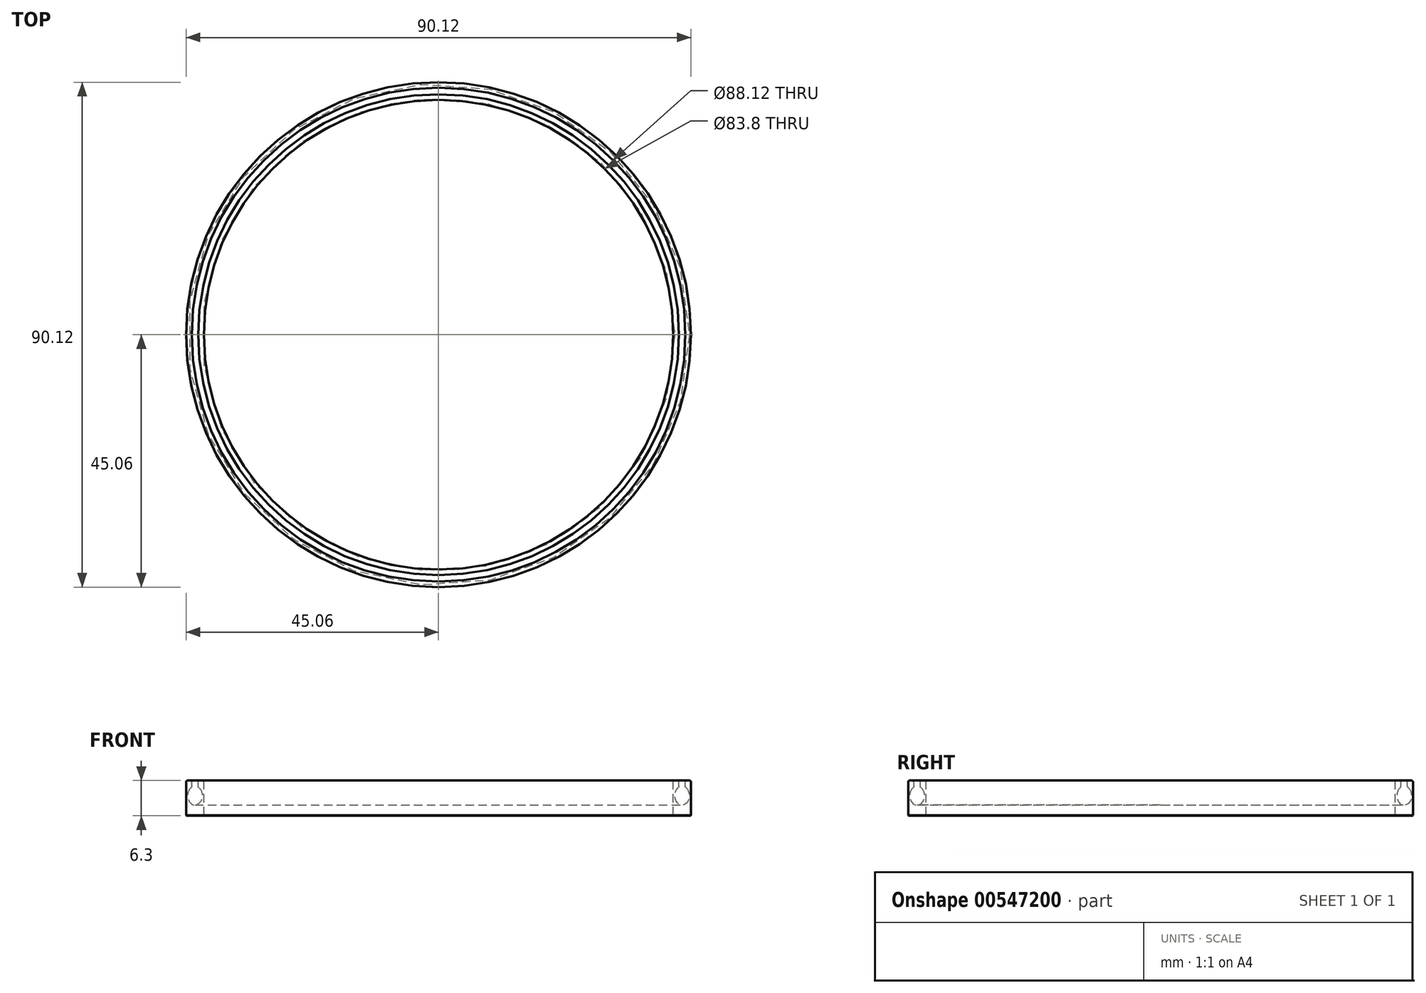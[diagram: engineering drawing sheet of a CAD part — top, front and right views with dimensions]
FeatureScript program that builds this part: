
annotation { "Feature Type Name" : "Feature", "Feature Type Description" : "" }
export const myFeature = defineFeature(function(context is Context, id is Id, definition is map)
    precondition{}
    {
        {
            var Q0;
            Q0=qCreatedBy(makeId("Front.planeOp"),FACE);
            var sketch = newSketch(context, id + "F0", { "sketchPlane" : qUnion([Q0])});
            skLineSegment(sketch, "E0.bottom", {"start": v(-41.9, -3.15) * mm, "end": v(-45.06, -3.15) * mm});
            skLineSegment(sketch, "E0.top", {"start": v(-41.9, 3.15) * mm, "end": v(-45.06, 3.15) * mm});
            skLineSegment(sketch, "E0.left", {"start": v(-41.9, -3.15) * mm, "end": v(-41.9, 3.15) * mm});
            skLineSegment(sketch, "E0.right", {"start": v(-45.06, -3.15) * mm, "end": v(-45.06, 3.15) * mm});
            skPoint(sketch, "E0.middle", {"position": v(-43.48, 0) * mm});
            skLineSegment(sketch, "E1", {"start": v(-45.06, 1.95) * mm, "end": v(-41.9, 1.95) * mm});
            skLineSegment(sketch, "E2", {"start": v(-44.06, 3.15) * mm, "end": v(-44.06, 1.95) * mm});
            skPoint(sketch, "E2.endSnap0", {"position": v(-43.48, 1.95) * mm});
            skLineSegment(sketch, "E3", {"start": v(-42.9, 3.15) * mm, "end": v(-42.9, 1.95) * mm});
            skEllipse(sketch, "E4", {"center": v(-43.48, 0.45) * mm, "majorRadius": 1.7 * mm, "minorRadius": 1.3 * mm, "majorAxis": v(0, -1)});
            skLineSegment(sketch, "E5", {"start": v(0, 9.73) * mm, "end": v(0, -12.45) * mm});
            skSolve(sketch);
        }
        {
            var Q0;
            {var subQ0=sQuery(id+"F0.wireOp",EDGE,"E0.right");var subQ1=sQuery(id+"F0.wireOp",EDGE,"E0.top");var subQ2=makeQuery(id+"F0.imprint","INTERSECT",VERTEX,{"derivedFrom":[subQ1,subQ0]});Q0=makeQuery(id+"F0.imprint","IMPRINT",FACE,{"disambiguationData":[TD([[makeQuery(id+"F0.imprint","IMPRINT",EDGE,{"disambiguationData":[TD([[subQ2,1.0]])],"derivedFrom":subQ1}),1.0]])]});}
            var Q1;
            {var subQ1=sQuery(id+"F0.wireOp",EDGE,"E0.left");var subQ5=sQuery(id+"F0.wireOp",EDGE,"E0.top");var subQ6=makeQuery(id+"F0.imprint","INTERSECT",VERTEX,{"derivedFrom":[subQ5,subQ1]});Q1=makeQuery(id+"F0.imprint","IMPRINT",FACE,{"disambiguationData":[TD([[makeQuery(id+"F0.imprint","IMPRINT",EDGE,{"disambiguationData":[TD([[subQ6,-1.0]])],"derivedFrom":subQ5}),1.0]])]});}
            var Q2;
            {var subQ5=sQuery(id+"F0.wireOp",EDGE,"E0.bottom");Q2=makeQuery(id+"F0.imprint","IMPRINT",FACE,{"disambiguationData":[TD([[makeQuery(id+"F0.imprint","IMPRINT",EDGE,{"derivedFrom":subQ5}),-1.0]])]});}
            var Q3;
            Q3=sQuery(id+"F0.wireOp",EDGE,"E5");
            revolve(context, id + "F1", {"entities" : qUnion([Q0, Q1, Q2]), "axis" : qUnion([Q3]), "revolveType" : RevolveType.FULL});
        }
        {
            var Q0;
            Q0=makeQuery(id+"F1.opRevolve","SWEPT_EDGE",EDGE,{"disambiguationData":[OSD([sQuery(id+"F0.wireOp",EDGE,"E0.top"),sQuery(id+"F0.wireOp",EDGE,"E0.right")])]});
            var Q1;
            Q1=makeQuery(id+"F1.opRevolve","SWEPT_EDGE",EDGE,{"disambiguationData":[OSD([sQuery(id+"F0.wireOp",EDGE,"E0.top"),sQuery(id+"F0.wireOp",EDGE,"E2")])]});
            var Q2;
            Q2=makeQuery(id+"F1.opRevolve","SWEPT_EDGE",EDGE,{"disambiguationData":[OSD([sQuery(id+"F0.wireOp",EDGE,"E0.top"),sQuery(id+"F0.wireOp",EDGE,"E3")])]});
            var Q3;
            Q3=makeQuery(id+"F1.opRevolve","SWEPT_EDGE",EDGE,{"disambiguationData":[OSD([sQuery(id+"F0.wireOp",EDGE,"E0.top"),sQuery(id+"F0.wireOp",EDGE,"E0.left")])]});
            var Q4;
            Q4=makeQuery(id+"F1.opRevolve","SWEPT_EDGE",EDGE,{"disambiguationData":[OSD([sQuery(id+"F0.wireOp",EDGE,"E2"),sQuery(id+"F0.wireOp",EDGE,"E4")])]});
            var Q5;
            Q5=makeQuery(id+"F1.opRevolve","SWEPT_EDGE",EDGE,{"disambiguationData":[OSD([sQuery(id+"F0.wireOp",EDGE,"E3"),sQuery(id+"F0.wireOp",EDGE,"E4")])]});
            fillet(context, id + "F2", {"entities" : qUnion([Q0, Q1, Q2, Q3, Q4, Q5]), "radius" : 0.3 * mm, "tangentPropagation" : true, "allowEdgeOverflow" : false});
        }
        {
            var Q0;
            Q0=makeQuery(id+"F1.opRevolve","SWEPT_EDGE",EDGE,{"disambiguationData":[OSD([sQuery(id+"F0.wireOp",EDGE,"E0.bottom"),sQuery(id+"F0.wireOp",EDGE,"E0.right")])]});
            var Q1;
            Q1=makeQuery(id+"F1.opRevolve","SWEPT_EDGE",EDGE,{"disambiguationData":[OSD([sQuery(id+"F0.wireOp",EDGE,"E0.bottom"),sQuery(id+"F0.wireOp",EDGE,"E0.left")])]});
            chamfer(context, id + "F3", {"entities" : qUnion([Q0, Q1]), "width" : 0.1 * mm, "tangentPropagation" : true});
        }
    });
